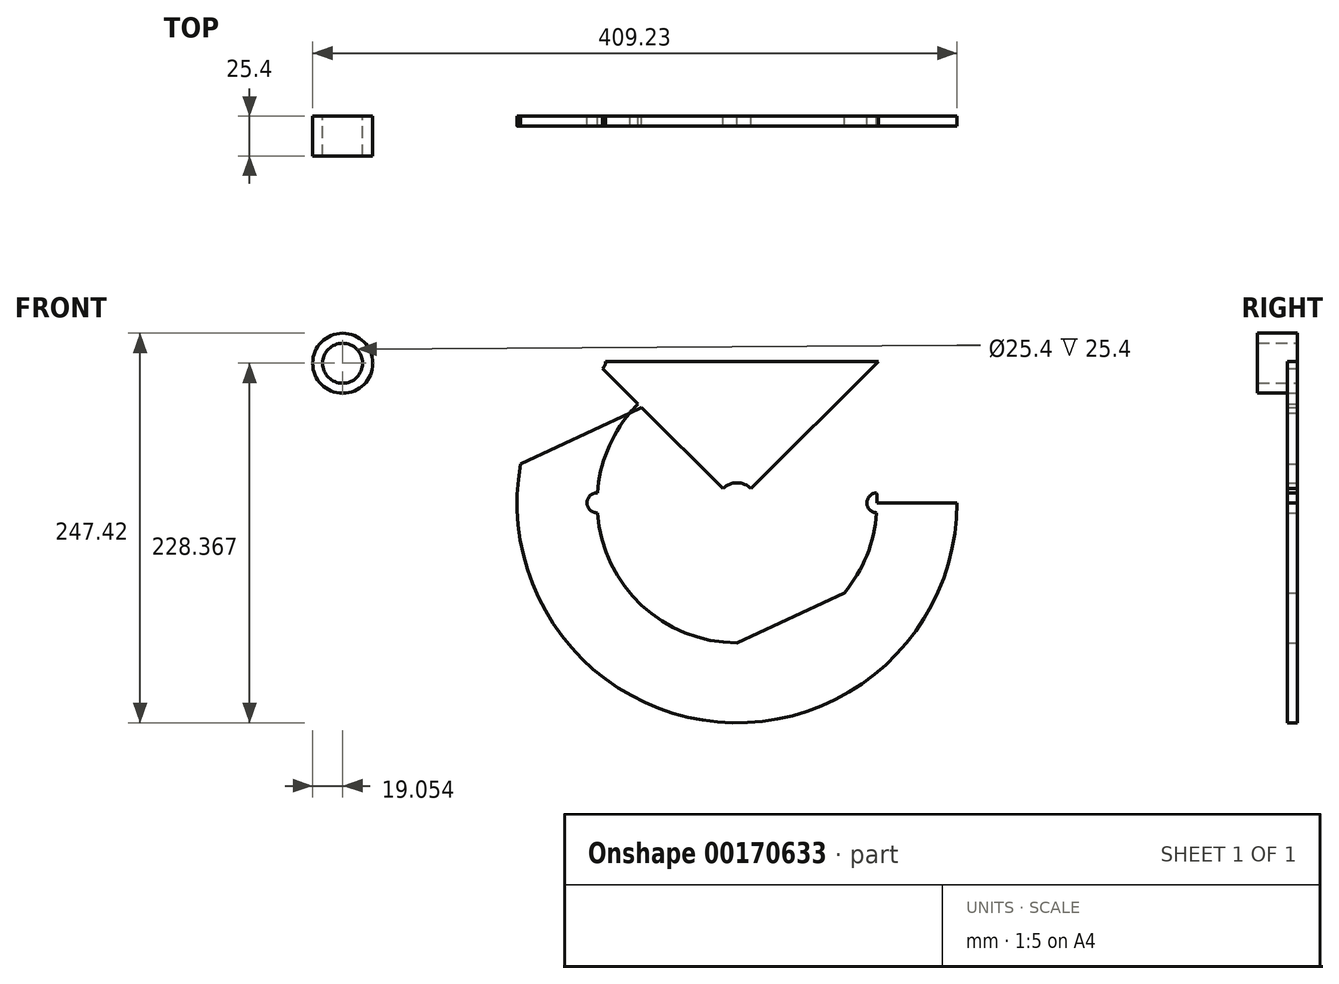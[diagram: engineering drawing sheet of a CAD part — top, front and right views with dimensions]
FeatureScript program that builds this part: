
annotation { "Feature Type Name" : "Feature", "Feature Type Description" : "" }
export const myFeature = defineFeature(function(context is Context, id is Id, definition is map)
    precondition{}
    {
        {
            var Q0;
            Q0=qCreatedBy(makeId("Front.planeOp"),FACE);
            var sketch = newSketch(context, id + "F0", { "sketchPlane" : qUnion([Q0])});
            skCircle(sketch, "E0", {"center": v(0, 0) * mm, "radius": 88.9 * mm});
            skLineSegment(sketch, "E1", {"start": v(-88.9, 0) * mm, "end": v(-292.1, 0) * mm});
            skLineSegment(sketch, "E2", {"start": v(0, -133.07) * mm, "end": v(0, 156.3) * mm, "construction": true});
            skLineSegment(sketch, "E3", {"start": v(-292.1, 0) * mm, "end": v(-190.5, 0) * mm});
            skLineSegment(sketch, "E4", {"start": v(-190.5, 0) * mm, "end": v(0, 88.9) * mm});
            skLineSegment(sketch, "E5", {"start": v(0, 0) * mm, "end": v(-89.8, 89.8) * mm});
            skLineSegment(sketch, "E6.MirrorCS", {"start": v(0, 0) * mm, "end": v(89.8, 89.8) * mm});
            skLineSegment(sketch, "E7", {"start": v(-89.8, 89.8) * mm, "end": v(89.8, 89.8) * mm});
            skLineSegment(sketch, "E8.MirrorCS", {"start": v(88.9, 0) * mm, "end": v(292.1, 0) * mm});
            skLineSegment(sketch, "E9.MirrorCS", {"start": v(190.5, 0) * mm, "end": v(0, -88.9) * mm});
            skCircle(sketch, "E10", {"center": v(0, 0) * mm, "radius": 139.7 * mm});
            skCircle(sketch, "E11", {"center": v(-89.8, 89.8) * mm, "radius": 6.35 * mm});
            skCircle(sketch, "E12", {"center": v(-88.9, 0) * mm, "radius": 6.35 * mm});
            skCircle(sketch, "E13", {"center": v(88.9, 0) * mm, "radius": 6.35 * mm});
            skCircle(sketch, "E14", {"center": v(0, 0) * mm, "radius": 12.7 * mm});
            skSolve(sketch);
        }
        {
            var Q0;
            {var subQ1=sQuery(id+"F0.wireOp",EDGE,"E0");var subQ11=sQuery(id+"F0.wireOp",EDGE,"E13");var subQ12=makeQuery(id+"F0.imprint","INTERSECT",VERTEX,{"disambiguationData":[OD(0.0)],"derivedFrom":[subQ1,subQ11]});Q0=makeQuery(id+"F0.imprint","IMPRINT",FACE,{"disambiguationData":[TD([[makeQuery(id+"F0.imprint","IMPRINT",EDGE,{"disambiguationData":[TD([[subQ12,-1.0]])],"derivedFrom":subQ1}),-1.0]])]});}
            var sketch = newSketch(context, id + "F1", { "sketchPlane" : qUnion([Q0])});
            skSolve(sketch);
        }
        {
            var Q0;
            Q0 = qSketchRegion(id + "F1", true);
            var Q1;
            {var subQ1=sQuery(id+"F0.wireOp",EDGE,"E0");var subQ11=sQuery(id+"F0.wireOp",EDGE,"E13");var subQ12=makeQuery(id+"F0.imprint","INTERSECT",VERTEX,{"disambiguationData":[OD(0.0)],"derivedFrom":[subQ1,subQ11]});Q1=makeQuery(id+"F0.imprint","IMPRINT",FACE,{"disambiguationData":[TD([[makeQuery(id+"F0.imprint","IMPRINT",EDGE,{"disambiguationData":[TD([[subQ12,-1.0]])],"derivedFrom":subQ1}),-1.0]])]});}
            var Q2;
            {var subQ1=sQuery(id+"F0.wireOp",EDGE,"E4");var subQ3=sQuery(id+"F0.wireOp",EDGE,"E0");var subQ4=makeQuery(id+"F0.imprint","INTERSECT",VERTEX,{"disambiguationData":[OD(1.0)],"derivedFrom":[subQ3,subQ1]});Q2=makeQuery(id+"F0.imprint","IMPRINT",FACE,{"disambiguationData":[TD([[makeQuery(id+"F0.imprint","IMPRINT",EDGE,{"disambiguationData":[TD([[subQ4,-1.0]])],"derivedFrom":subQ3}),-1.0]])]});}
            var Q3;
            {var subQ1=sQuery(id+"F0.wireOp",EDGE,"E9.MirrorCS");var subQ3=sQuery(id+"F0.wireOp",EDGE,"E0");var subQ5=makeQuery(id+"F0.imprint","INTERSECT",VERTEX,{"disambiguationData":[OD(0.0)],"derivedFrom":[subQ3,subQ1]});Q3=makeQuery(id+"F0.imprint","IMPRINT",FACE,{"disambiguationData":[TD([[makeQuery(id+"F0.imprint","IMPRINT",EDGE,{"disambiguationData":[TD([[subQ5,1.0]])],"derivedFrom":subQ3}),-1.0]])]});}
            var Q4;
            {var subQ1=sQuery(id+"F0.wireOp",EDGE,"E0");var subQ4=sQuery(id+"F0.wireOp",EDGE,"E13");var subQ5=makeQuery(id+"F0.imprint","INTERSECT",VERTEX,{"disambiguationData":[OD(0.0)],"derivedFrom":[subQ1,subQ4]});Q4=makeQuery(id+"F0.imprint","IMPRINT",FACE,{"disambiguationData":[TD([[makeQuery(id+"F0.imprint","IMPRINT",EDGE,{"disambiguationData":[TD([[subQ5,-1.0]])],"derivedFrom":subQ1}),1.0]])]});}
            var Q5;
            {var subQ3=sQuery(id+"F0.wireOp",EDGE,"E0");var subQ9=makeQuery(id+"F0.imprint","INTERSECT",VERTEX,{"disambiguationData":[OD(0.0)],"derivedFrom":[subQ3,sQuery(id+"F0.wireOp",EDGE,"E4")]});Q5=makeQuery(id+"F0.imprint","IMPRINT",FACE,{"disambiguationData":[TD([[makeQuery(id+"F0.imprint","IMPRINT",EDGE,{"disambiguationData":[TD([[subQ9,1.0]])],"derivedFrom":subQ3}),-1.0]])]});}
            var Q6;
            {var subQ3=sQuery(id+"F0.wireOp",EDGE,"E0");var subQ9=makeQuery(id+"F0.imprint","INTERSECT",VERTEX,{"disambiguationData":[OD(0.0)],"derivedFrom":[subQ3,sQuery(id+"F0.wireOp",EDGE,"E4")]});Q6=makeQuery(id+"F0.imprint","IMPRINT",FACE,{"disambiguationData":[TD([[makeQuery(id+"F0.imprint","IMPRINT",EDGE,{"disambiguationData":[TD([[subQ9,1.0]])],"derivedFrom":subQ3}),-1.0]])]});}
            var Q7;
            {var subQ3=sQuery(id+"F0.wireOp",EDGE,"E9.MirrorCS");var subQ5=sQuery(id+"F0.wireOp",EDGE,"E0");var subQ6=makeQuery(id+"F0.imprint","INTERSECT",VERTEX,{"disambiguationData":[OD(1.0)],"derivedFrom":[subQ5,subQ3]});Q7=makeQuery(id+"F0.imprint","IMPRINT",FACE,{"disambiguationData":[TD([[makeQuery(id+"F0.imprint","IMPRINT",EDGE,{"disambiguationData":[TD([[subQ6,-1.0]])],"derivedFrom":subQ5}),-1.0]])]});}
            var Q8;
            {var subQ0=sQuery(id+"F0.wireOp",EDGE,"E9.MirrorCS");var subQ1=sQuery(id+"F0.wireOp",EDGE,"E0");var subQ2=makeQuery(id+"F0.imprint","INTERSECT",VERTEX,{"disambiguationData":[OD(0.0)],"derivedFrom":[subQ1,subQ0]});Q8=makeQuery(id+"F0.imprint","IMPRINT",FACE,{"disambiguationData":[TD([[makeQuery(id+"F0.imprint","IMPRINT",EDGE,{"disambiguationData":[TD([[subQ2,-1.0]])],"derivedFrom":subQ1}),1.0]])]});}
            var Q9;
            {var subQ1=sQuery(id+"F0.wireOp",EDGE,"E0");var subQ5=sQuery(id+"F0.wireOp",EDGE,"E4");var subQ6=makeQuery(id+"F0.imprint","INTERSECT",VERTEX,{"disambiguationData":[OD(0.0)],"derivedFrom":[subQ1,subQ5]});Q9=makeQuery(id+"F0.imprint","IMPRINT",FACE,{"disambiguationData":[TD([[makeQuery(id+"F0.imprint","IMPRINT",EDGE,{"disambiguationData":[TD([[subQ6,1.0]])],"derivedFrom":subQ1}),1.0]])]});}
            var Q10;
            {var subQ0=sQuery(id+"F0.wireOp",EDGE,"E4");var subQ1=sQuery(id+"F0.wireOp",EDGE,"E0");var subQ2=makeQuery(id+"F0.imprint","INTERSECT",VERTEX,{"disambiguationData":[OD(0.0)],"derivedFrom":[subQ1,subQ0]});Q10=makeQuery(id+"F0.imprint","IMPRINT",FACE,{"disambiguationData":[TD([[makeQuery(id+"F0.imprint","IMPRINT",EDGE,{"disambiguationData":[TD([[subQ2,-1.0]])],"derivedFrom":subQ1}),1.0]])]});}
            var Q11;
            {var subQ0=sQuery(id+"F0.wireOp",EDGE,"E5");var subQ1=sQuery(id+"F0.wireOp",EDGE,"E0");var subQ2=makeQuery(id+"F0.imprint","INTERSECT",VERTEX,{"derivedFrom":[subQ1,subQ0]});Q11=makeQuery(id+"F0.imprint","IMPRINT",FACE,{"disambiguationData":[TD([[makeQuery(id+"F0.imprint","IMPRINT",EDGE,{"disambiguationData":[TD([[subQ2,-1.0]])],"derivedFrom":subQ1}),1.0]])]});}
            extrude(context, id + "F2", {"entities" : qUnion([Q0, Q1, Q2, Q3, Q4, Q5, Q6, Q7, Q8, Q9, Q10, Q11]), "depth" : 6.35 * mm});
        }
        {
            var Q0;
            Q0=qCreatedBy(makeId("Front.planeOp"),FACE);
            var sketch = newSketch(context, id + "F3", { "sketchPlane" : qUnion([Q0])});
            skCircle(sketch, "E15", {"center": v(-250.48, 88.67) * mm, "radius": 19.05 * mm});
            skCircle(sketch, "E16", {"center": v(-250.48, 88.67) * mm, "radius": 12.7 * mm});
            skSolve(sketch);
        }
        {
            var Q0;
            Q0 = qSketchRegion(id + "F3", true);
            extrude(context, id + "F4", {"entities" : qUnion([Q0]), "depth" : 25.4 * mm});
        }
    });
